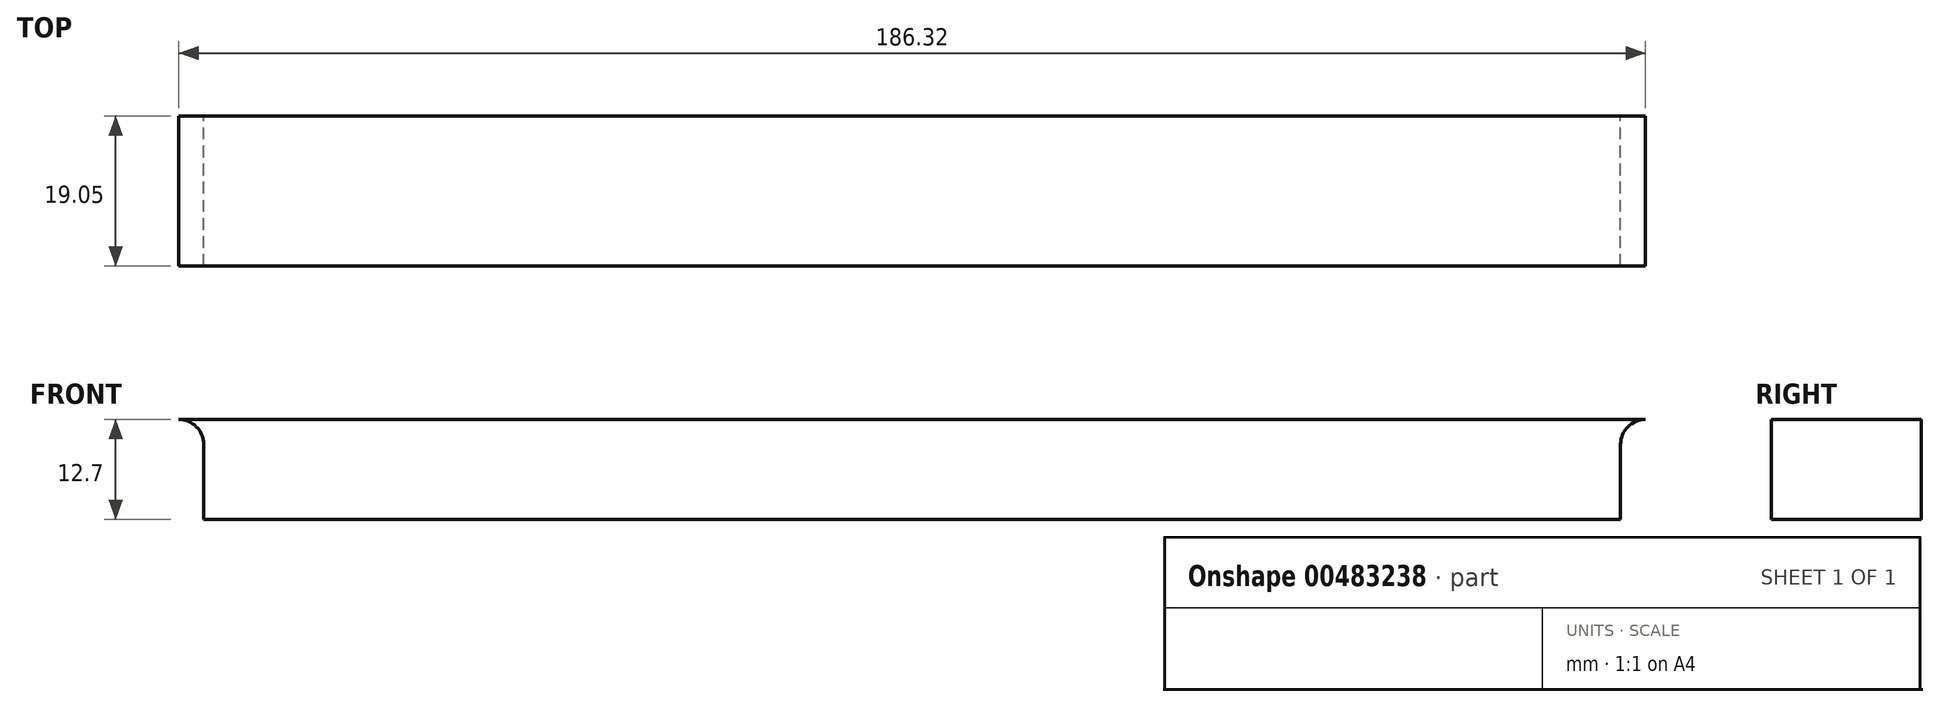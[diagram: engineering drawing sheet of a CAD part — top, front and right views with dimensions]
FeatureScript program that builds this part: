
annotation { "Feature Type Name" : "Feature", "Feature Type Description" : "" }
export const myFeature = defineFeature(function(context is Context, id is Id, definition is map)
    precondition{}
    {
        {
            var Q0;
            Q0=qCreatedBy(makeId("Front.planeOp"),FACE);
            var sketch = newSketch(context, id + "F0", { "sketchPlane" : qUnion([Q0])});
            skLineSegment(sketch, "E0.bottom", {"start": v(118.56, 6.35) * mm, "end": v(-67.76, 6.35) * mm});
            skLineSegment(sketch, "E0.top", {"start": v(115.39, -6.35) * mm, "end": v(-64.59, -6.35) * mm});
            skPoint(sketch, "E0.middle", {"position": v(0, 0) * mm});
            skLineSegment(sketch, "E1", {"start": v(-64.59, 3.18) * mm, "end": v(-64.59, -6.35) * mm});
            skLineSegment(sketch, "E2", {"start": v(115.39, 3.17) * mm, "end": v(115.39, -6.35) * mm});
            skArc(sketch, "E3", {"start": v(118.56, 6.35) * mm, "mid": v(116.32, 5.42) * mm, "end": v(115.39, 3.17) * mm});
            skPoint(sketch, "E4.orphan", {"position": v(67.76, -6.35) * mm});
            skArc(sketch, "E5", {"start": v(-64.59, 3.18) * mm, "mid": v(-65.52, 5.42) * mm, "end": v(-67.76, 6.35) * mm});
            skPoint(sketch, "E6.orphan", {"position": v(-118.56, -6.35) * mm});
            skSolve(sketch);
        }
        {
            var Q0;
            Q0=qSketchRegion(id+"F0",true);
            extrude(context, id + "F1", {"entities" : qUnion([Q0]), "depth" : 19.05 * mm});
        }
    });
